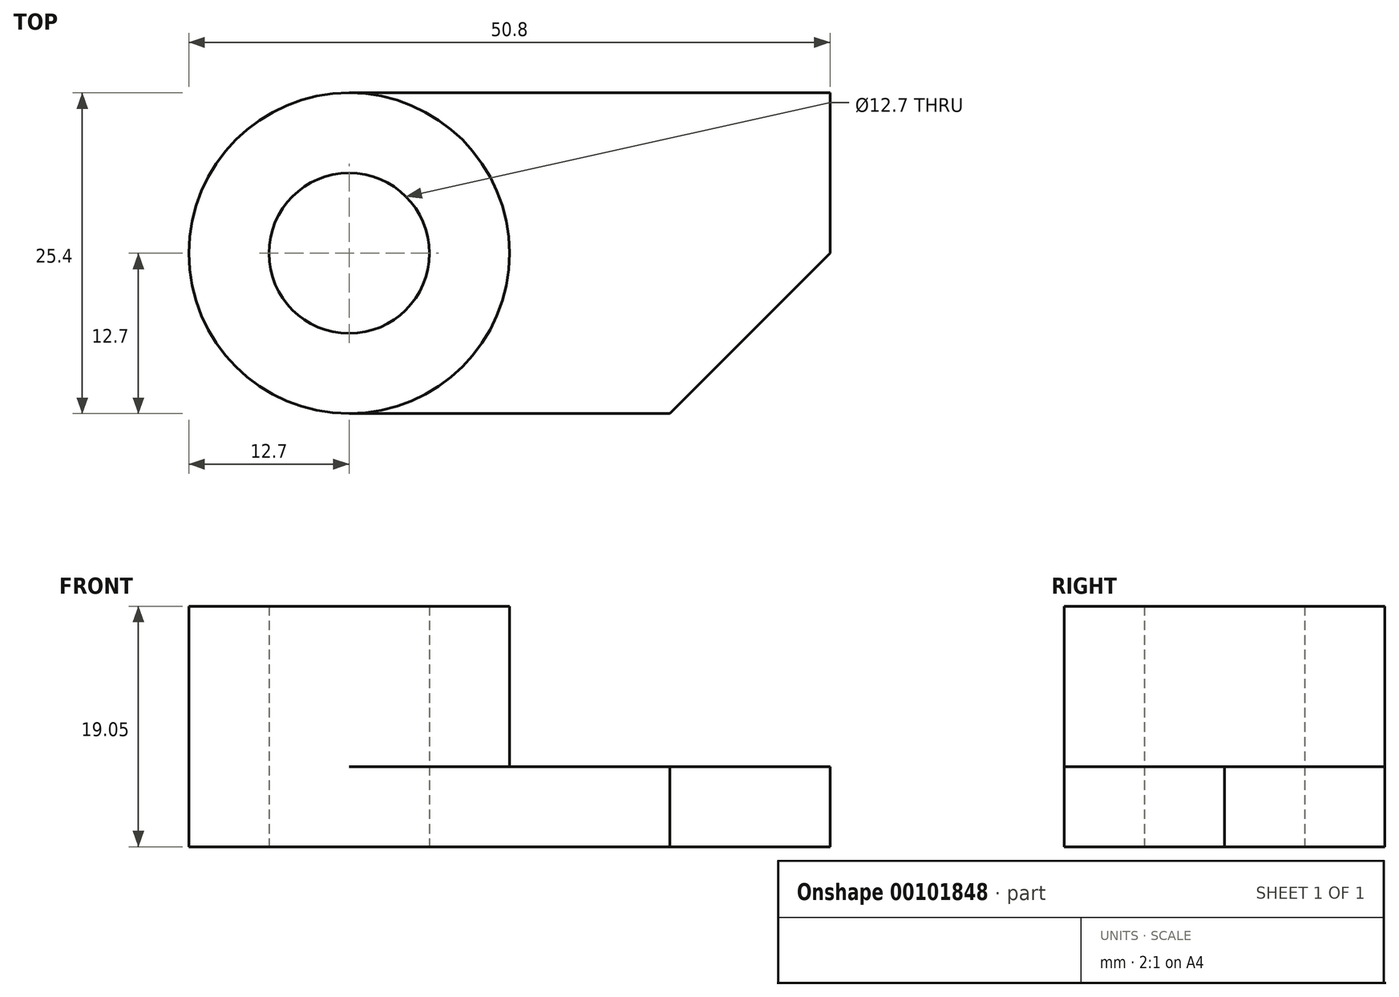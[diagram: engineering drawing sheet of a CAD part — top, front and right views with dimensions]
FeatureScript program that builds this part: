
annotation { "Feature Type Name" : "Feature", "Feature Type Description" : "" }
export const myFeature = defineFeature(function(context is Context, id is Id, definition is map)
    precondition{}
    {
        {
            var Q0;
            Q0=qCreatedBy(makeId("Top.planeOp"),FACE);
            var sketch = newSketch(context, id + "F0", { "sketchPlane" : qUnion([Q0])});
            skCircle(sketch, "E0", {"center": v(0, 0) * mm, "radius": 12.7 * mm});
            skCircle(sketch, "E1", {"center": v(0, 0) * mm, "radius": 6.35 * mm});
            skSolve(sketch);
        }
        {
            var Q0;
            Q0=makeQuery(id+"F0.imprint","IMPRINT",FACE,{"disambiguationData":[TD([[makeQuery(id+"F0.imprint","IMPRINT",EDGE,{"derivedFrom":sQuery(id+"F0.wireOp",EDGE,"E0")}),1.0]])]});
            extrude(context, id + "F1", {"entities" : qUnion([Q0]), "depth" : 19.05 * mm});
        }
        {
            var Q0;
            Q0=qCreatedBy(makeId("Right.planeOp"),FACE);
            cPlane(context, id + "F2", {"entities" : qUnion([Q0]), "cplaneType" : CPlaneType.OFFSET, "offset" : 38.1 * mm, "width" : 152.4 * mm, "height" : 152.4 * mm});
        }
        {
            var Q0;
            Q0=qCreatedBy(id+"F2.planeOp",FACE);
            var sketch = newSketch(context, id + "F3", { "sketchPlane" : qUnion([Q0])});
            skLineSegment(sketch, "E2", {"start": v(-12.7, 0) * mm, "end": v(-12.7, 6.35) * mm});
            skLineSegment(sketch, "E3", {"start": v(-12.7, 6.35) * mm, "end": v(12.7, 6.35) * mm});
            skLineSegment(sketch, "E4", {"start": v(12.7, 6.35) * mm, "end": v(12.7, 0) * mm});
            skLineSegment(sketch, "E5", {"start": v(12.7, 0) * mm, "end": v(-12.7, 0) * mm});
            skSolve(sketch);
        }
        {
            var Q0;
            Q0 = qSketchRegion(id + "F3", true);
            extrude(context, id + "F4", {"entities" : qUnion([Q0]), "operationType" : NewBodyOperationType.ADD, "endBound" : BoundingType.UP_TO_NEXT, "oppositeDirection" : true, "depth" : 25.4 * mm});
        }
        {
            var Q0;
            Q0=makeQuery(id+"F4.boolean.opBoolean","MERGE",FACE,{"derivedFrom":[makeQuery(id+"F1.opExtrude","CAP_FACE",FACE,{"disambiguationData":[OSD([sQuery(id+"F0.wireOp",EDGE,"E0"),sQuery(id+"F0.wireOp",EDGE,"E1")])],"isStart":true}),makeQuery(id+"F4.opExtrude","SWEPT_FACE",FACE,{"disambiguationData":[OSD([sQuery(id+"F3.wireOp",EDGE,"E5")])]})]});
            var sketch = newSketch(context, id + "F5", { "sketchPlane" : qUnion([Q0])});
            skLineSegment(sketch, "E6", {"start": v(38.1, 0) * mm, "end": v(25.4, 12.7) * mm});
            skSolve(sketch);
        }
        {
            var Q0;
            {var subQ0=sQuery(id+"F5.wireOp",EDGE,"E6");Q0=makeQuery(id+"F5.imprint","IMPRINT",FACE,{"disambiguationData":[TD([[makeQuery(id+"F5.imprint","IMPRINT",EDGE,{"derivedFrom":subQ0}),-1.0]])]});}
            extrude(context, id + "F6", {"entities" : qUnion([Q0]), "operationType" : NewBodyOperationType.REMOVE, "endBound" : BoundingType.THROUGH_ALL, "oppositeDirection" : true, "depth" : 25.4 * mm});
        }
    });
